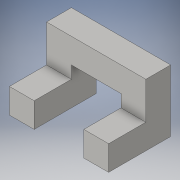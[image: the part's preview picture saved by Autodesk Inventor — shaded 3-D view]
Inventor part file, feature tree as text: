
AUTODESK INVENTOR PART (.ipt)
format: ipt  version: 2016 (Build 200138000, 138)  size: 112,128 bytes
history: native  units: in
note: dims shown in document units (in); Inventor stores cm internally (conversion verified against a paired STEP export)
features: extrude x3, sketch x3
ambient origin geometry x8: Origin, YZ Plane, XZ Plane, XY Plane, X Axis, Y Axis, Z Axis, Center Point
bodies: Solid1 (feature_tree)
feature tree (6):
  extrude  "Extrusion1"  Depth=1.25in
  extrude  "Extrusion2"  Depth=0.5in
  extrude  "Extrusion3"  Depth=0.75in
  sketch  "Sketch1"  dims[d0=2.0in d1=1.25in]
  sketch  "Sketch2"  dims[d2=1.25in d3=0.0in d4=0.5in]
  sketch  "Sketch3"  dims[d5=0.5in d6=0.75in d7=1.25in d8=0.0in d9=0.75in d10=0.75in d11=2.0in d12=0.0in]
